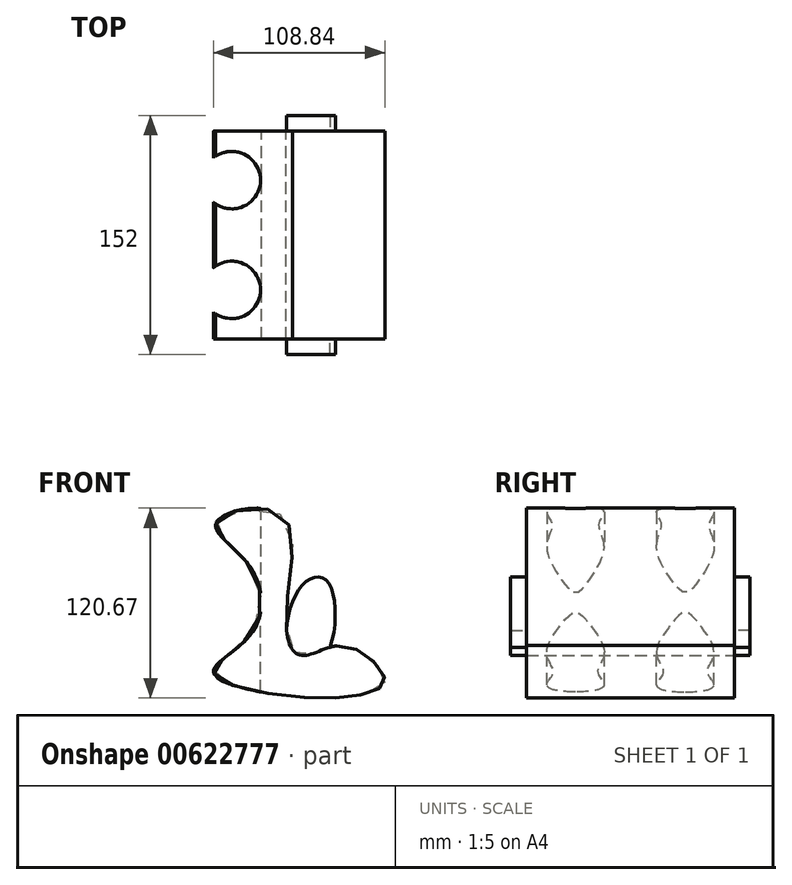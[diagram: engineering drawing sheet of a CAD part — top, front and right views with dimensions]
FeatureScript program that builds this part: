
annotation { "Feature Type Name" : "Feature", "Feature Type Description" : "" }
export const myFeature = defineFeature(function(context is Context, id is Id, definition is map)
    precondition{}
    {
        {
            var Q0;
            Q0=qCreatedBy(makeId("Front.planeOp"),FACE);
            var sketch = newSketch(context, id + "F0", { "sketchPlane" : qUnion([Q0])});
            skFitSpline(sketch, "E0", {"points": [v(13.9, -23.04) * mm, v(36.06, -31.48) * mm, v(44.5, -45.9) * mm, v(31.13, -53.64) * mm, v(-18.47, -54.7) * mm, v(-64.2, -39.57) * mm, v(-39.93, -14.95) * mm, v(-42.04, 28.67) * mm, v(-62.44, 55.4) * mm, v(-21.28, 60.33) * mm, v(-18.12, -4.05) * mm, v(-8.97, -29.02) * mm, v(13.9, -23.04) * mm]});
            skSolve(sketch);
        }
        {
            var Q0;
            Q0 = qSketchRegion(id + "F0", true);
            extrude(context, id + "F1", {"entities" : qUnion([Q0]), "depth" : 66 * mm, "offsetDistance" : 25 * mm});
        }
        {
            var Q0;
            Q0=qCreatedBy(makeId("Top.planeOp"),FACE);
            var sketch = newSketch(context, id + "F2", { "sketchPlane" : qUnion([Q0])});
            skCircle(sketch, "E1", {"center": v(-52.53, -34.86) * mm, "radius": 18.25 * mm});
            skSolve(sketch);
        }
        {
            var Q0;
            Q0=makeQuery(id+"F2.imprint","IMPRINT",FACE,{"disambiguationData":[TD([[makeQuery(id+"F2.imprint","IMPRINT",EDGE,{"derivedFrom":sQuery(id+"F2.wireOp",EDGE,"E1")}),1.0]])]});
            extrude(context, id + "F3", {"entities" : qUnion([Q0]), "operationType" : NewBodyOperationType.REMOVE, "oppositeDirection" : true, "depth" : 100 * mm, "offsetDistance" : 25 * mm});
        }
        {
            var Q0;
            Q0 = qSketchRegion(id + "F2", true);
            var Q1;
            Q1 = qConstructionFilter(qBodyType(qCreatedBy(id + "F2" ,EDGE), BodyType.WIRE), ConstructionObject.NO);
            extrude(context, id + "F4", {"entities" : qUnion([Q0]), "operationType" : NewBodyOperationType.REMOVE, "surfaceEntities" : qUnion([Q1]), "depth" : 91.4 * mm, "offsetDistance" : 25 * mm});
        }
        {
            var Q0;
            Q0=makeQuery(id+"F1.opExtrude","CAP_FACE",FACE,{"disambiguationData":[OSD([sQuery(id+"F0.wireOp",EDGE,"E0")])],"isStart":false});
            var sketch = newSketch(context, id + "F5", { "sketchPlane" : qUnion([Q0])});
            skFitSpline(sketch, "E2", {"points": [v(5.01, -33.3) * mm, v(8.38, 17.72) * mm, v(-9.41, 13.44) * mm, v(-13.88, -33.35) * mm, v(5.01, -33.3) * mm]});
            skSolve(sketch);
        }
        {
            var Q0;
            {var subQ0=sQuery(id+"F5.wireOp",EDGE,"E2");var subQ1=makeQuery(id+"F1.opExtrude","CAP_EDGE",EDGE,{"disambiguationData":[OSD([sQuery(id+"F0.wireOp",EDGE,"E0")])],"isStart":false});var subQ2=makeQuery(id+"F5.imprint","INTERSECT",VERTEX,{"disambiguationData":[OD(0.0)],"derivedFrom":[subQ1,subQ0]});Q0=makeQuery(id+"F5.imprint","IMPRINT",FACE,{"disambiguationData":[TD([[makeQuery(id+"F5.imprint","IMPRINT",EDGE,{"disambiguationData":[TD([[subQ2,1.0]])],"derivedFrom":subQ0}),1.0]])]});}
            extrude(context, id + "F6", {"entities" : qUnion([Q0]), "depth" : 10 * mm, "offsetDistance" : 25 * mm});
        }
        {
            var Q0;
            Q0=makeQuery(id+"F1.opExtrude","SWEPT_BODY",BODY,{"disambiguationData":[OSD([sQuery(id+"F0.wireOp",EDGE,"E0")])]});
            var Q1;
            Q1=makeQuery(id+"F6.opExtrude","SWEPT_BODY",BODY,{"disambiguationData":[OSD([sQuery(id+"F0.wireOp",EDGE,"E0"),sQuery(id+"F5.wireOp",EDGE,"E2")])]});
            var Q2;
            Q2=qCreatedBy(makeId("Front.planeOp"),FACE);
            mirror(context, id + "F7", {"operationType" : NewBodyOperationType.ADD, "entities" : qUnion([Q0, Q1]), "mirrorPlane" : qUnion([Q2])});
        }
    });
